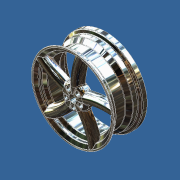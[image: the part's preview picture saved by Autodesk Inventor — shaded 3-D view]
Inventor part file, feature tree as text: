
AUTODESK INVENTOR PART (.ipt)
format: ipt  version: unknown  size: 1,553,408 bytes
history: native  units: mm (DEFAULTED — no unit token found)
features: fillet x14, sketch x10, pattern_circular x4, revolve x3, extrude x3, other x2, plane x1, sweep x1, hole x1, chamfer x1
ambient origin geometry x5: Origin, YZ Plane, XZ Plane, XY Plane, Center Point
feature tree (40):
  sketch  "Sketch1"  dims[d0=457.2mm d1=90.0deg]
  other  "Work Point1"
  revolve  "Revolution1"  Angle=90.0deg
  other  "Work Axis3"
  plane  "Work Plane1"
  sweep  "Sweep1"
  pattern_circular  "Circular Pattern2"  Count=2  [1 undecoded]
  revolve  "Revolution5"  [1 undecoded]
  fillet  "Fillet3"  Radius=50.0mm
  fillet  "Fillet4"  Radius=18.0mm
  fillet  "Fillet5"  Radius=10.0mm
  revolve  "Revolution6"  [1 undecoded]
  fillet  "Fillet6"  Radius=2.0mm
  fillet  "Fillet7"  Radius=2.0mm
  extrude  "Extrusion1"  Depth=2.0mm
  pattern_circular  "Circular Pattern3"  [2 undecoded]
  extrude  "Extrusion2"  Depth=2.0mm
  extrude  "Extrusion3"  Depth=2.0mm
  fillet  "Fillet8"  Radius=2.0mm
  fillet  "Fillet9"  [1 undecoded]
  pattern_circular  "Circular Pattern4"  [2 undecoded]
  pattern_circular  "Circular Pattern5"  [2 undecoded]
  fillet  "Fillet10"  [1 undecoded]
  fillet  "Fillet11"  [1 undecoded]
  hole  "Hole1"  [1 undecoded]
  chamfer  "Chamfer1"  [1 undecoded]
  fillet  "Fillet12"  [1 undecoded]
  fillet  "Fillet13"  [1 undecoded]
  fillet  "Fillet14"  [1 undecoded]
  fillet  "Fillet15"  [1 undecoded]
  fillet  "Fillet16"  [1 undecoded]
  sketch  "Sketch3"  dims[d2=45.0deg d11=0.0mm d12=50.0mm d14=12.566371mm]
  sketch  "Sketch8"  dims[d20=0.0mm]
  sketch  "Sketch9"  dims[d21=90.0deg]
  sketch  "Sketch11"  dims[d22=5.0mm]
  sketch  "Sketch12"  dims[d23=5.0mm]
  sketch  "Sketch13"  dims[d24=5.0mm]
  sketch  "Sketch15"  dims[d25=90.0deg d26=20.0mm]
  sketch  "Sketch16"  dims[d27=8.0mm d28=10.0mm d29=0.0mm d30=50.0mm d32=12.566371mm d33=18.0mm d34=0.0mm d35=10.0mm d36=-0.872665mm]
  sketch  "Sketch17"  dims[d37=3.0mm d38=3.0mm d39=50.0mm d41=12.566371mm d42=50.0mm d44=12.566371mm d45=1.0mm d46=2.0mm d47=38.1mm d48=4.0mm d49=2.0mm d50=60.0deg d51=8.0mm d52=0.0mm d53=2.0mm d54=2.0mm d55=2.0mm d56=2.0mm d57=2.0mm d58=2.0mm d59=2.0mm d60=45.0deg]
note: 19 required parameter values undecoded (feature->parameter linkage not recoverable at this tier; creation-order binding heuristic only, values carry confidence <= 0.55)